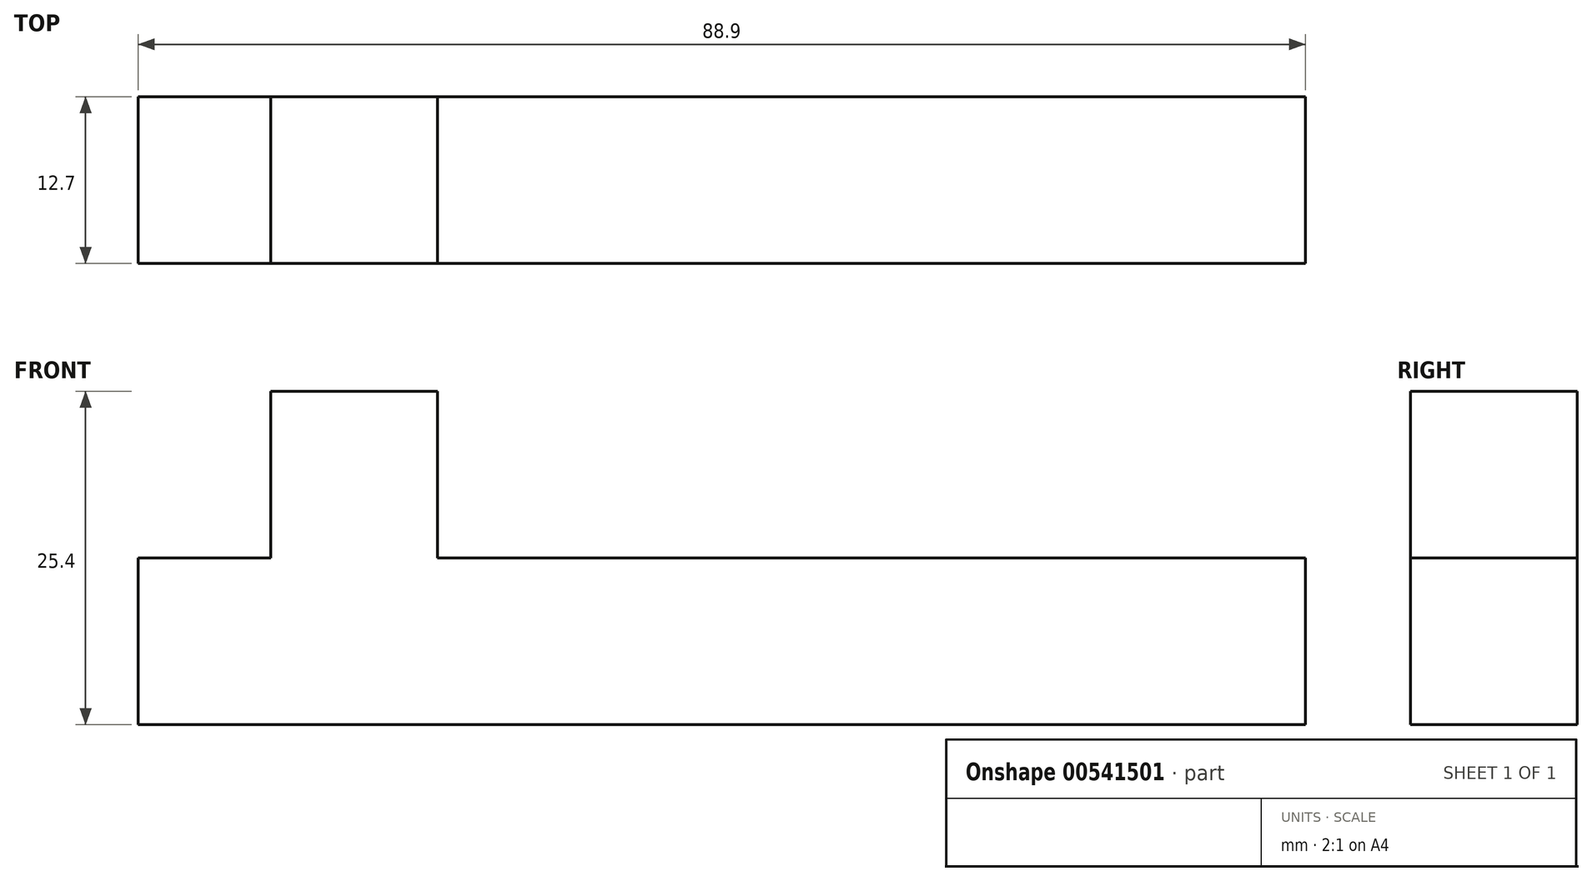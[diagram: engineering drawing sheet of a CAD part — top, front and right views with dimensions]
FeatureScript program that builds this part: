
annotation { "Feature Type Name" : "Feature", "Feature Type Description" : "" }
export const myFeature = defineFeature(function(context is Context, id is Id, definition is map)
    precondition{}
    {
        {
            var Q0;
            Q0=qCreatedBy(makeId("Top.planeOp"),FACE);
            var sketch = newSketch(context, id + "F0", { "sketchPlane" : qUnion([Q0])});
            skLineSegment(sketch, "E0", {"start": v(-73.45, 0) * mm, "end": v(-73.45, 12.7) * mm});
            skLineSegment(sketch, "E1", {"start": v(-73.45, 12.7) * mm, "end": v(15.45, 12.7) * mm});
            skLineSegment(sketch, "E2", {"start": v(15.45, 12.7) * mm, "end": v(15.45, 0) * mm});
            skLineSegment(sketch, "E3", {"start": v(15.45, 0) * mm, "end": v(-73.45, 0) * mm});
            skSolve(sketch);
        }
        {
            var Q0;
            Q0 = qSketchRegion(id + "F0", true);
            extrude(context, id + "F1", {"entities" : qUnion([Q0]), "depth" : 12.7 * mm, "offsetDistance" : 25.4 * mm});
        }
        {
            var Q0;
            Q0=makeQuery(id+"F1.opExtrude","CAP_FACE",FACE,{"disambiguationData":[OSD([sQuery(id+"F0.wireOp",EDGE,"E0"),sQuery(id+"F0.wireOp",EDGE,"E1"),sQuery(id+"F0.wireOp",EDGE,"E2"),sQuery(id+"F0.wireOp",EDGE,"E3")])],"isStart":false});
            var sketch = newSketch(context, id + "F2", { "sketchPlane" : qUnion([Q0])});
            skSolve(sketch);
        }
        {
            var Q0;
            Q0=makeQuery(id+"F2.imprint","IMPRINT",FACE,{"disambiguationData":[TD([[makeQuery(id+"F2.imprint","IMPRINT",EDGE,{"derivedFrom":makeQuery(id+"F1.opExtrude","CAP_EDGE",EDGE,{"disambiguationData":[OSD([sQuery(id+"F0.wireOp",EDGE,"E0")])],"isStart":false})}),-1.0]])]});
            var sketch = newSketch(context, id + "F3", { "sketchPlane" : qUnion([Q0])});
            skLineSegment(sketch, "E4.bottom", {"start": v(-63.36, 0) * mm, "end": v(-50.66, 0) * mm});
            skLineSegment(sketch, "E4.top", {"start": v(-63.36, 12.7) * mm, "end": v(-50.66, 12.7) * mm});
            skLineSegment(sketch, "E4.left", {"start": v(-63.36, 0) * mm, "end": v(-63.36, 12.7) * mm});
            skLineSegment(sketch, "E4.right", {"start": v(-50.66, 0) * mm, "end": v(-50.66, 12.7) * mm});
            skSolve(sketch);
        }
        {
            var Q0;
            Q0 = qSketchRegion(id + "F3", true);
            extrude(context, id + "F4", {"entities" : qUnion([Q0]), "operationType" : NewBodyOperationType.ADD, "depth" : 12.7 * mm, "offsetDistance" : 25.4 * mm});
        }
    });
